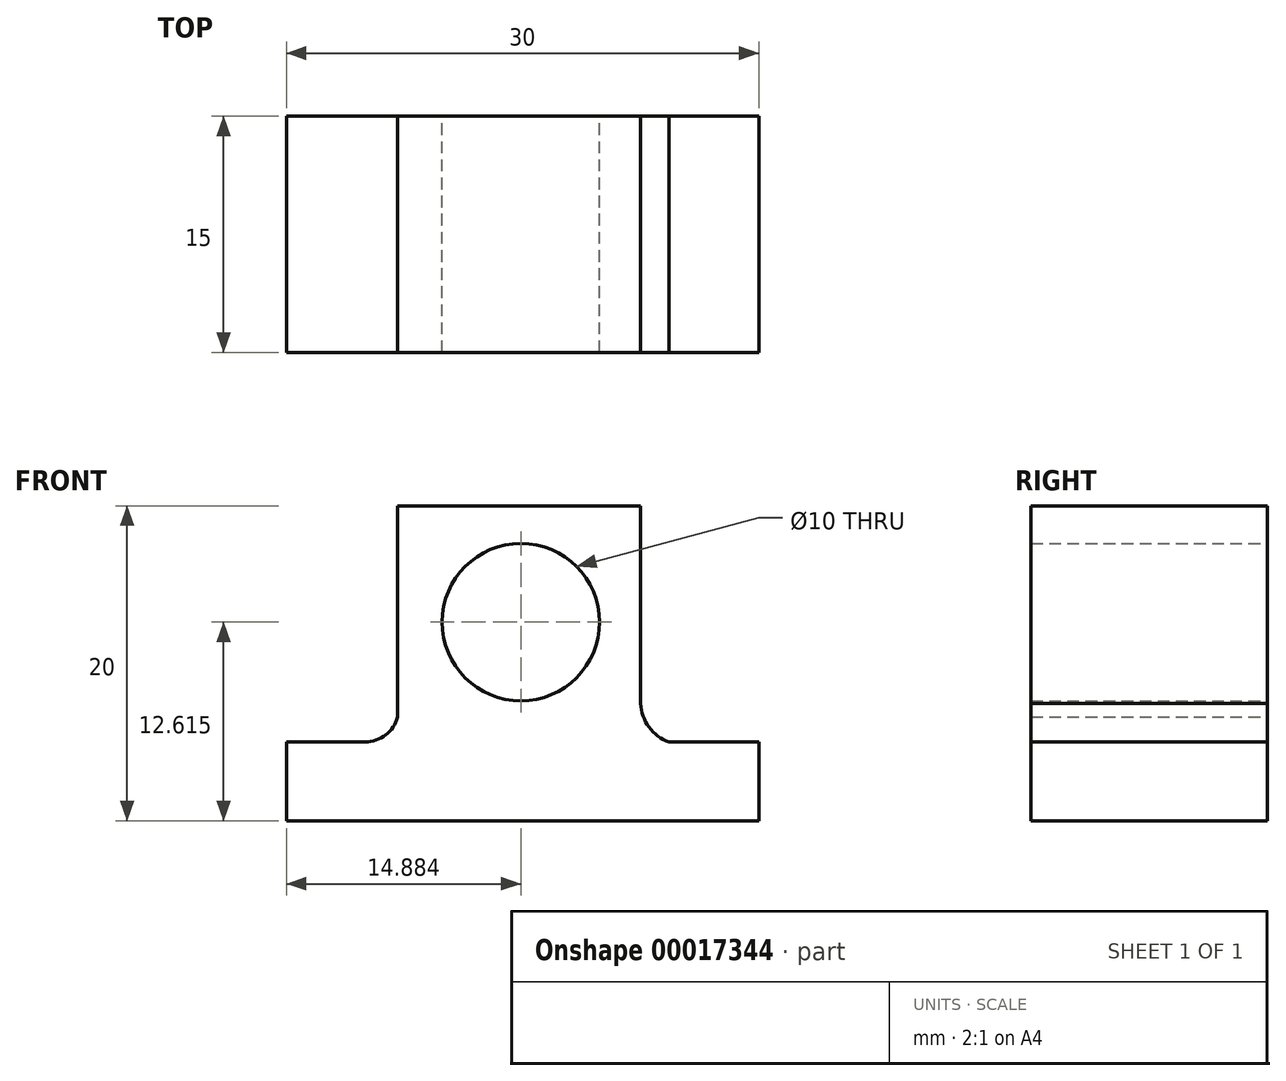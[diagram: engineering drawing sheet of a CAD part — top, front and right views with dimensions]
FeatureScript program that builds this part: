
annotation { "Feature Type Name" : "Feature", "Feature Type Description" : "" }
export const myFeature = defineFeature(function(context is Context, id is Id, definition is map)
    precondition{}
    {
        {
            var Q0;
            Q0=qCreatedBy(makeId("Front.planeOp"),FACE);
            var sketch = newSketch(context, id + "F0", { "sketchPlane" : qUnion([Q0])});
            skLineSegment(sketch, "E0", {"start": v(-20.37, -24.92) * mm, "end": v(-20.37, -29.92) * mm});
            skLineSegment(sketch, "E1", {"start": v(-20.37, -29.92) * mm, "end": v(9.63, -29.92) * mm});
            skLineSegment(sketch, "E2", {"start": v(9.63, -29.92) * mm, "end": v(9.63, -24.92) * mm});
            skLineSegment(sketch, "E3", {"start": v(9.63, -24.92) * mm, "end": v(2.13, -24.92) * mm});
            skLineSegment(sketch, "E4", {"start": v(2.13, -24.92) * mm, "end": v(2.13, -9.92) * mm});
            skLineSegment(sketch, "E5", {"start": v(2.13, -9.92) * mm, "end": v(-13.32, -9.92) * mm});
            skLineSegment(sketch, "E6", {"start": v(-13.32, -9.92) * mm, "end": v(-13.32, -24.92) * mm});
            skLineSegment(sketch, "E7", {"start": v(-13.32, -24.92) * mm, "end": v(-20.37, -24.92) * mm});
            skCircle(sketch, "E8", {"center": v(-5.49, -17.3) * mm, "radius": 5 * mm});
            skArc(sketch, "E9", {"start": v(2.13, -22.25) * mm, "mid": v(2.59, -23.88) * mm, "end": v(3.92, -24.92) * mm});
            skLineSegment(sketch, "E10", {"start": v(2.13, -22.25) * mm, "end": v(-13.32, -22.25) * mm});
            skLineSegment(sketch, "E11", {"start": v(3.92, -24.92) * mm, "end": v(3.92, -29.92) * mm});
            skLineSegment(sketch, "E12", {"start": v(3.92, -24.92) * mm, "end": v(9.63, -24.92) * mm});
            skLineSegment(sketch, "E13.bottom", {"start": v(-20.37, -24.92) * mm, "end": v(-15.37, -24.92) * mm});
            skLineSegment(sketch, "E13.top", {"start": v(-20.37, -29.92) * mm, "end": v(-15.37, -29.92) * mm});
            skLineSegment(sketch, "E13.right", {"start": v(-15.37, -24.92) * mm, "end": v(-15.37, -29.92) * mm});
            skArc(sketch, "E14", {"start": v(-15.37, -24.92) * mm, "mid": v(-13.7, -24.1) * mm, "end": v(-13.32, -22.25) * mm});
            skSolve(sketch);
        }
        {
            var Q0;
            Q0 = qSketchRegion(id + "F0", true);
            extrude(context, id + "F1", {"entities" : qUnion([Q0]), "depth" : 15 * mm});
        }
    });
